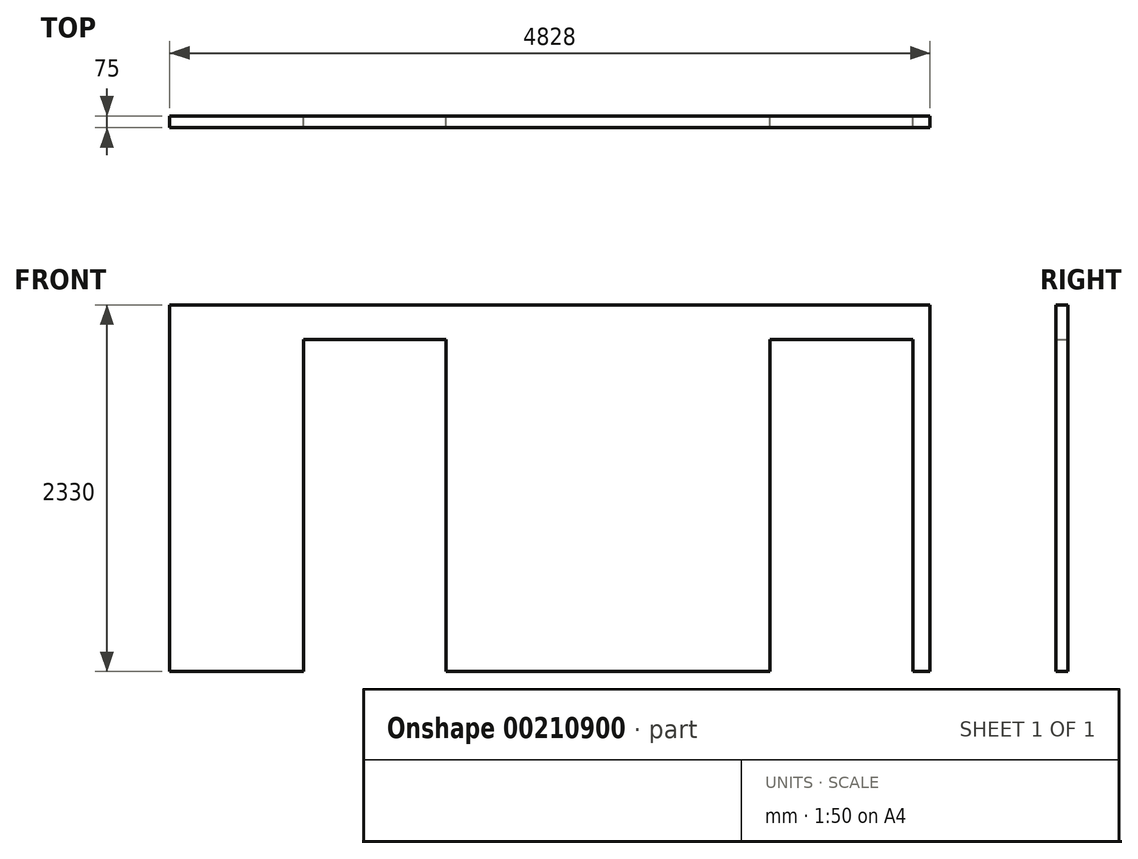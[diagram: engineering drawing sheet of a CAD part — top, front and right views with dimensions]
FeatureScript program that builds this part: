
annotation { "Feature Type Name" : "Feature", "Feature Type Description" : "" }
export const myFeature = defineFeature(function(context is Context, id is Id, definition is map)
    precondition{}
    {
        {
            var Q0;
            Q0=qCreatedBy(makeId("Front.planeOp"),FACE);
            var sketch = newSketch(context, id + "F0", { "sketchPlane" : qUnion([Q0])});
            skLineSegment(sketch, "E0.bottom", {"start": v(0, 0) * mm, "end": v(4828, 0) * mm});
            skLineSegment(sketch, "E0.top", {"start": v(0, 2330) * mm, "end": v(4828, 2330) * mm});
            skLineSegment(sketch, "E0.left", {"start": v(0, 0) * mm, "end": v(0, 2330) * mm});
            skLineSegment(sketch, "E0.right", {"start": v(4828, 0) * mm, "end": v(4828, 2330) * mm});
            skLineSegment(sketch, "E1.bottom", {"start": v(850, 0) * mm, "end": v(1755, 0) * mm});
            skLineSegment(sketch, "E1.top", {"start": v(850, 2110) * mm, "end": v(1755, 2110) * mm});
            skLineSegment(sketch, "E1.left", {"start": v(850, 0) * mm, "end": v(850, 2110) * mm});
            skLineSegment(sketch, "E1.right", {"start": v(1755, 0) * mm, "end": v(1755, 2110) * mm});
            skLineSegment(sketch, "E2.bottom", {"start": v(3813, 0) * mm, "end": v(4718, 0) * mm});
            skLineSegment(sketch, "E2.top", {"start": v(3813, 2110) * mm, "end": v(4718, 2110) * mm});
            skLineSegment(sketch, "E2.left", {"start": v(3813, 0) * mm, "end": v(3813, 2110) * mm});
            skLineSegment(sketch, "E2.right", {"start": v(4718, 0) * mm, "end": v(4718, 2110) * mm});
            skSolve(sketch);
        }
        {
            var Q0;
            Q0=makeQuery(id+"F0.imprint","IMPRINT",FACE,{"disambiguationData":[TD([[makeQuery(id+"F0.imprint","IMPRINT",EDGE,{"derivedFrom":sQuery(id+"F0.wireOp",EDGE,"E0.bottom")}),1.0]])]});
            extrude(context, id + "F1", {"entities" : qUnion([Q0]), "depth" : 75 * mm});
        }
    });
